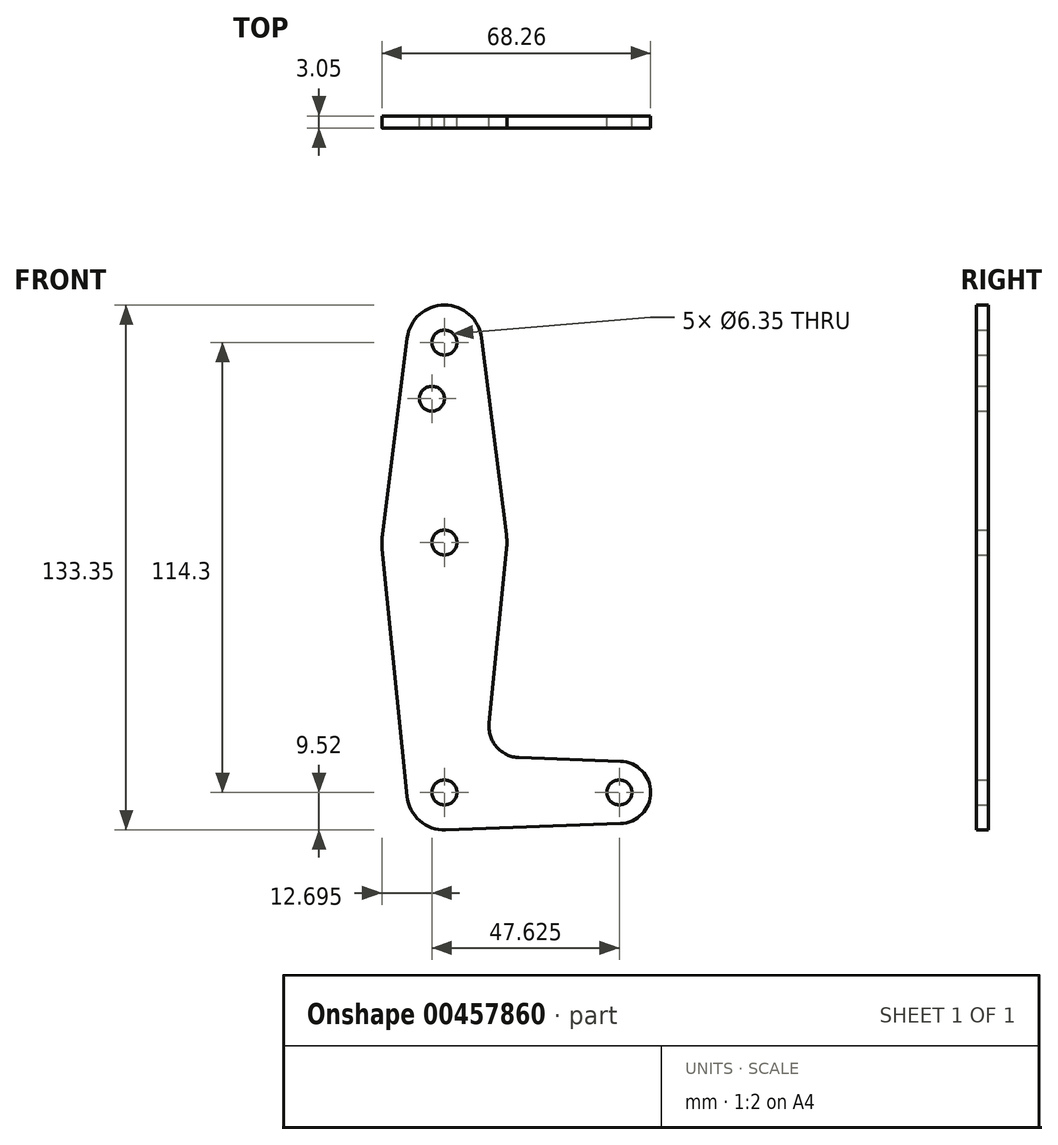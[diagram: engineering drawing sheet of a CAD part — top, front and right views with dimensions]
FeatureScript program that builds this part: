
annotation { "Feature Type Name" : "Feature", "Feature Type Description" : "" }
export const myFeature = defineFeature(function(context is Context, id is Id, definition is map)
    precondition{}
    {
        {
            var Q0;
            Q0=qCreatedBy(makeId("Front.planeOp"),FACE);
            var sketch = newSketch(context, id + "F0", { "sketchPlane" : qUnion([Q0])});
            skCircle(sketch, "E0", {"center": v(0, 114.3) * mm, "radius": 9.53 * mm});
            skCircle(sketch, "E1", {"center": v(0, 63.5) * mm, "radius": 15.88 * mm});
            skCircle(sketch, "E2", {"center": v(44.45, 0) * mm, "radius": 7.94 * mm});
            skLineSegment(sketch, "E3", {"start": v(0, 114.3) * mm, "end": v(0, 63.5) * mm, "construction": true});
            skLineSegment(sketch, "E4", {"start": v(0, 63.5) * mm, "end": v(0, 0) * mm, "construction": true});
            skLineSegment(sketch, "E5", {"start": v(0, 0) * mm, "end": v(44.45, 0) * mm, "construction": true});
            skCircle(sketch, "E6", {"center": v(0, 114.3) * mm, "radius": 3.17 * mm});
            skCircle(sketch, "E7", {"center": v(0, 63.5) * mm, "radius": 3.18 * mm});
            skCircle(sketch, "E8", {"center": v(0, 0) * mm, "radius": 3.18 * mm});
            skCircle(sketch, "E9", {"center": v(44.45, 0) * mm, "radius": 3.18 * mm});
            skCircle(sketch, "E10", {"center": v(-3.17, 100.03) * mm, "radius": 3.18 * mm});
            skLineSegment(sketch, "E11", {"start": v(-9.45, 115.5) * mm, "end": v(-15.75, 65.48) * mm});
            skLineSegment(sketch, "E12.MirrorCS", {"start": v(9.45, 115.5) * mm, "end": v(15.75, 65.48) * mm});
            skCircle(sketch, "E13", {"center": v(0, 0) * mm, "radius": 9.53 * mm});
            skLineSegment(sketch, "E14", {"start": v(-15.8, 61.91) * mm, "end": v(-9.48, -0.95) * mm});
            skLineSegment(sketch, "E15", {"start": v(18.97, 8.85) * mm, "end": v(44.73, 7.93) * mm});
            skLineSegment(sketch, "E16", {"start": v(0.34, -9.52) * mm, "end": v(44.73, -7.93) * mm});
            skLineSegment(sketch, "E17.MirrorCS", {"start": v(15.8, 61.91) * mm, "end": v(11.34, 17.6) * mm});
            skPoint(sketch, "E18.newPointA", {"position": v(9.48, -0.95) * mm});
            skArc(sketch, "E18.filletArc", {"start": v(11.34, 17.6) * mm, "mid": v(13.26, 11.57) * mm, "end": v(18.97, 8.85) * mm});
            skSolve(sketch);
        }
        {
            var Q0;
            Q0 = qSketchRegion(id + "F0", true);
            extrude(context, id + "F1", {"entities" : qUnion([Q0]), "depth" : 3.05 * mm});
        }
    });
